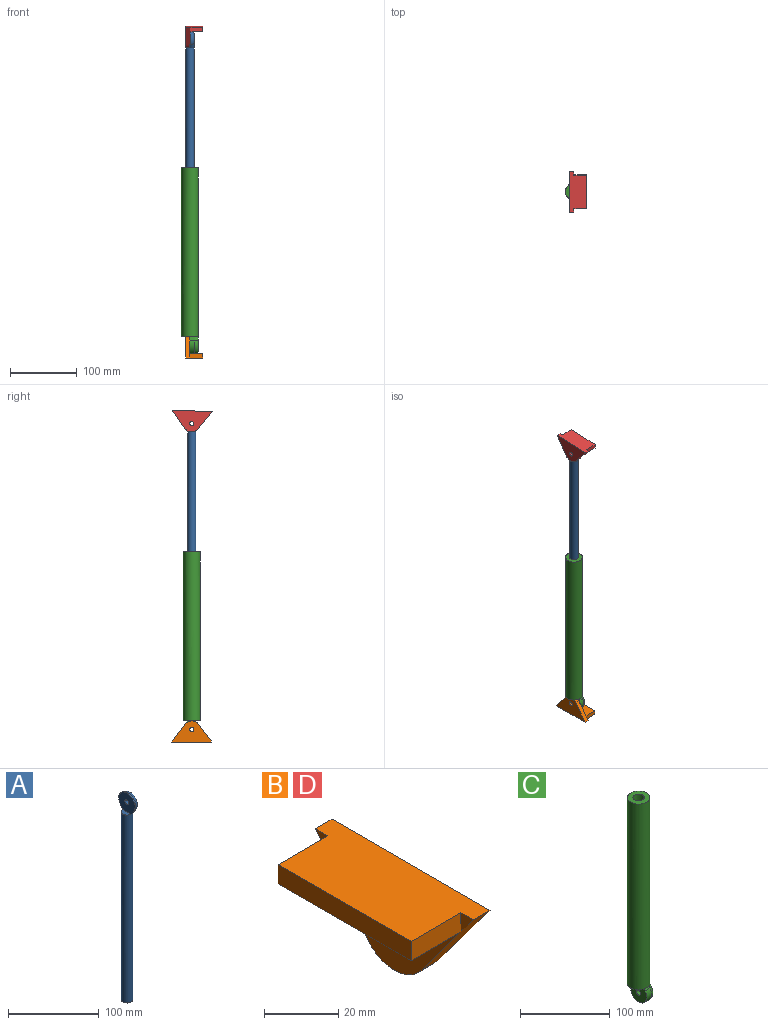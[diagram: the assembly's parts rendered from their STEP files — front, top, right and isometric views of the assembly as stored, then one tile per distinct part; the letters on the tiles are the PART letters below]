
ASSEMBLY  parts=4 mates=3
PART A: 14 faces, bbox 12.7x27.5x280.4 mm
  f0: plane 12.7x6.35mm, normal (0,0,1), area 63.3mm2, adj f1,f10
  f1: cylinder r=6.35mm len=254mm, axis (0,0,-1), area 10134.1mm2, adj f0,f2,f3,f4
  f2: plane 12.7x12.7mm, normal (0,0,-1), area 126.7mm2, adj f1
  f3: plane 6.35x6.35mm, normal (0,0,-1), area 1.7mm2, adj f1,f5,f11
  f4: plane 6.35x6.35mm, normal (0,0,-1), area 1.7mm2, adj f1,f7,f13
  f5: plane 5.08x3.81mm, normal (0,0.8,-0.6), area 8.1mm2, adj f3,f6,f10,f11
  f6: cylinder r=12.7mm len=25.4mm, axis (-1,0,0), area 71.4mm2, adj f5,f7,f10,f12
  f7: plane 5.08x3.81mm, normal (0,-0.8,-0.6), area 8.1mm2, adj f4,f6,f10,f13
  f8: cylinder r=3.17mm len=6.35mm, axis (-1,0,0), area 126.7mm2, adj f9,f10
  f9: plane 20.32x15.24mm, normal (1,0,0), area 174.3mm2, adj f8,f11,f12,f13
  f10: plane 25.4x25.4mm, normal (-1,0,0), area 486.8mm2, adj f0,f5,f6,f7,f8
  f11: cylinder r=5.08mm len=11.18mm, axis (0,-0.6,-0.8), area 61.7mm2, adj f3,f5,f9,f12
  f12: torus R=7.62mm, axis (1,0,0), area 383.6mm2, adj f6,f9,f11,f13
  f13: cylinder r=5.08mm len=11.18mm, axis (0,-0.6,0.8), area 61.7mm2, adj f4,f7,f9,f12
PART B: 13 faces, bbox 25.4x60.3x31.8 mm
  f0: plane 6.35x4.76mm, normal (-1,0,0), area 15.1mm2, adj f2,f5,f9
  f1: plane 6.35x4.76mm, normal (-1,0,0), area 15.1mm2, adj f4,f5,f11
  f2: plane 26.67x20mm, normal (0,0.8,-0.6), area 211.7mm2, adj f0,f3,f5,f7,f8
  f3: cylinder r=12.7mm len=20.32mm, axis (1,0,0), area 149.6mm2, adj f2,f4,f7,f8
  f4: plane 26.67x20mm, normal (0,-0.8,-0.6), area 211.7mm2, adj f1,f3,f5,f7,f8
  f5: plane 60.33x25.4mm, normal (0,0,1), area 1350.8mm2, adj f0,f1,f2,f4,f8,f9,f11,f12
  f6: cylinder r=3.17mm len=6.35mm, axis (1,0,0), area 126.7mm2, adj f7,f8
  f7: plane 50.8x25.4mm, normal (-1,0,0), area 763.1mm2, adj f2,f3,f4,f6,f10
  f8: plane 60.33x31.75mm, normal (1,0,0), area 1115.9mm2, adj f2,f3,f4,f5,f6
  f9: plane 19.05x6.35mm, normal (0,1,0), area 121mm2, adj f0,f5,f10,f12
  f10: plane 50.8x19.05mm, normal (0,0,-1), area 967.7mm2, adj f7,f9,f11,f12
  f11: plane 19.05x6.35mm, normal (0,-1,0), area 121mm2, adj f1,f5,f10,f12
  f12: plane 50.8x6.35mm, normal (-1,0,0), area 322.6mm2, adj f5,f9,f10,f11
PART C: 14 faces, bbox 25.4x27.5x280.4 mm
  f0: plane 25.4x25.4mm, normal (0,0,-1), area 295.9mm2, adj f1,f2,f4,f6,f11,f13
  f1: cylinder r=6.35mm len=254mm, axis (0,0,1), area 10134.1mm2, adj f0,f3,f8
  f2: cylinder r=12.7mm len=254mm, axis (0,0,1), area 20268.3mm2, adj f0,f3
  f3: plane 25.4x25.4mm, normal (0,0,1), area 380mm2, adj f1,f2
  f4: plane 7.62x5.08mm, normal (0,-0.8,0.6), area 48.4mm2, adj f0,f5,f10,f13
  f5: cylinder r=12.7mm len=25.4mm, axis (-1,0,0), area 428.6mm2, adj f4,f6,f10,f12
  f6: plane 7.62x5.08mm, normal (0,0.8,0.6), area 48.4mm2, adj f0,f5,f10,f11
  f7: cylinder r=3.17mm len=12.7mm, axis (-1,0,0), area 253.4mm2, adj f9,f10
  f8: plane 12.7x6.35mm, normal (0,0,1), area 63.3mm2, adj f1,f10
  f9: plane 20.32x15.24mm, normal (1,0,0), area 174.3mm2, adj f7,f11,f12,f13
  f10: plane 25.4x25.4mm, normal (-1,0,0), area 486.8mm2, adj f4,f5,f6,f7,f8
  f11: cylinder r=5.08mm len=11.18mm, axis (0,0.6,-0.8), area 61.7mm2, adj f0,f6,f9,f12
  f12: torus R=7.62mm, axis (1,0,0), area 383.6mm2, adj f5,f9,f11,f13
  f13: cylinder r=5.08mm len=11.18mm, axis (0,0.6,0.8), area 61.7mm2, adj f0,f4,f9,f12
PART D: same geometry as B
PLACE A t=(-95.88,-64.26,-68.25)mm
PLACE B rot(axis=(0,-1,0),180deg) t=(-102.23,-64.26,5.41)mm
PLACE C rot(axis=(0,0,1),0deg) t=(-95.88,-64.26,5.41)mm
PLACE D rot(axis=(0,0.02,-1),180deg) t=(-102.23,-52.43,-67.99)mm
MATE revolute B.f3 <-> C.f5  axis (1,0,0) through (-95.88,-64.26,-261.29)mm
MATE revolute D.f3 <-> A.f6  axis (-1,0,0) through (-95.88,-64.26,198.45)mm
MATE slider A.f1 <-> C.f1  axis (0,0,1) through (-95.88,-64.26,-68.25)mm
